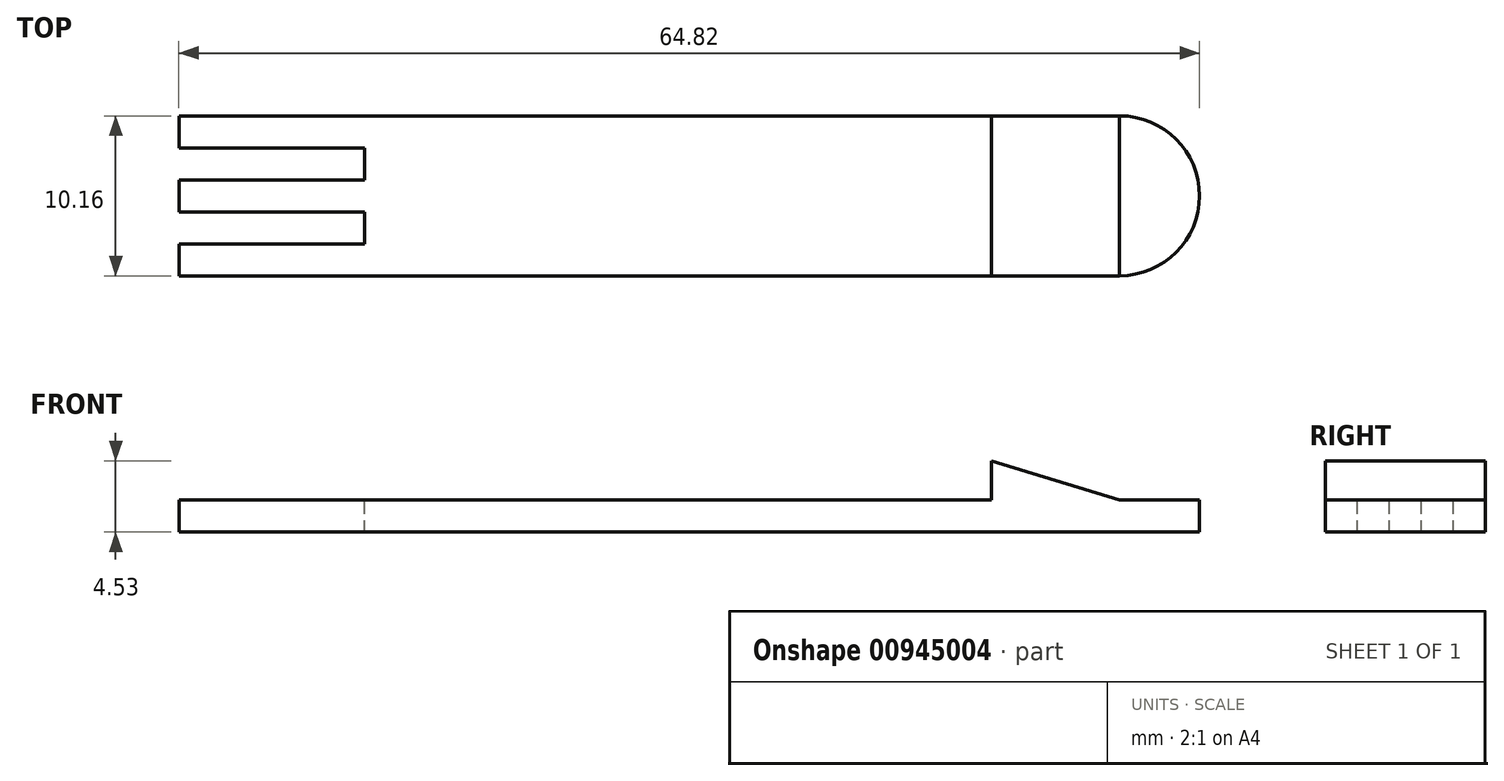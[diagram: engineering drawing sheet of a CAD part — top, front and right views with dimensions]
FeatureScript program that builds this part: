
annotation { "Feature Type Name" : "Feature", "Feature Type Description" : "" }
export const myFeature = defineFeature(function(context is Context, id is Id, definition is map)
    precondition{}
    {
        {
            var Q0;
            Q0=qCreatedBy(makeId("Top.planeOp"),FACE);
            var sketch = newSketch(context, id + "F0", { "sketchPlane" : qUnion([Q0])});
            skLineSegment(sketch, "E0.bottom", {"start": v(-19.76, -30.4) * mm, "end": v(39.98, -30.4) * mm});
            skLineSegment(sketch, "E0.top", {"start": v(-19.76, -40.55) * mm, "end": v(39.98, -40.55) * mm});
            skLineSegment(sketch, "E0.left", {"start": v(-19.76, -30.4) * mm, "end": v(-19.76, -40.55) * mm});
            skLineSegment(sketch, "E0.right", {"start": v(39.98, -30.4) * mm, "end": v(39.98, -40.55) * mm});
            skArc(sketch, "E1", {"start": v(39.98, -40.55) * mm, "mid": v(45.06, -35.47) * mm, "end": v(39.98, -30.4) * mm});
            skSolve(sketch);
        }
        {
            var Q0;
            Q0=qSketchRegion(id+"F0",true);
            extrude(context, id + "F1", {"entities" : qUnion([Q0]), "depth" : 2.03 * mm, "offsetDistance" : 25.4 * mm});
        }
        {
            var Q0;
            Q0=makeQuery(id+"F1.opExtrude","CAP_FACE",FACE,{"disambiguationData":[OSD([sQuery(id+"F0.wireOp",EDGE,"E0.bottom"),sQuery(id+"F0.wireOp",EDGE,"E0.top"),sQuery(id+"F0.wireOp",EDGE,"E0.left"),sQuery(id+"F0.wireOp",EDGE,"E1")])],"isStart":false});
            var sketch = newSketch(context, id + "F2", { "sketchPlane" : qUnion([Q0])});
            skLineSegment(sketch, "E2", {"start": v(-19.76, -32.42) * mm, "end": v(-7.97, -32.42) * mm});
            skLineSegment(sketch, "E3", {"start": v(-19.76, -32.42) * mm, "end": v(-19.76, -30.4) * mm});
            skLineSegment(sketch, "E4", {"start": v(-19.76, -30.4) * mm, "end": v(-19.76, -32.42) * mm});
            skLineSegment(sketch, "E5", {"start": v(-19.76, -34.45) * mm, "end": v(-7.97, -34.45) * mm});
            skLineSegment(sketch, "E6", {"start": v(-19.76, -34.45) * mm, "end": v(-19.76, -32.42) * mm});
            skLineSegment(sketch, "E7", {"start": v(-19.76, -36.49) * mm, "end": v(-7.97, -36.49) * mm});
            skLineSegment(sketch, "E8", {"start": v(-19.76, -36.49) * mm, "end": v(-19.76, -34.45) * mm});
            skLineSegment(sketch, "E9", {"start": v(-19.76, -38.52) * mm, "end": v(-7.97, -38.52) * mm});
            skLineSegment(sketch, "E10", {"start": v(-19.76, -38.52) * mm, "end": v(-19.76, -40.55) * mm});
            skLineSegment(sketch, "E11", {"start": v(-19.76, -40.55) * mm, "end": v(-19.76, -38.52) * mm});
            skLineSegment(sketch, "E12", {"start": v(-7.97, -32.42) * mm, "end": v(-7.97, -34.45) * mm});
            skLineSegment(sketch, "E13", {"start": v(-7.97, -36.49) * mm, "end": v(-7.97, -38.52) * mm});
            skSolve(sketch);
        }
        {
            var Q0;
            Q0=makeQuery(id+"F2.imprint","IMPRINT",FACE,{"disambiguationData":[TD([[makeQuery(id+"F2.imprint","IMPRINT",EDGE,{"derivedFrom":sQuery(id+"F2.wireOp",EDGE,"E2")}),-1.0]])]});
            var Q1;
            {var subQ0=sQuery(id+"F2.wireOp",EDGE,"E7");Q1=makeQuery(id+"F2.imprint","IMPRINT",FACE,{"disambiguationData":[TD([[makeQuery(id+"F2.imprint","IMPRINT",EDGE,{"derivedFrom":subQ0}),-1.0]])]});}
            extrude(context, id + "F3", {"entities" : qUnion([Q0, Q1]), "operationType" : NewBodyOperationType.REMOVE, "oppositeDirection" : true, "depth" : 25.4 * mm, "offsetDistance" : 25.4 * mm});
        }
        {
            var Q0;
            Q0=makeQuery(id+"F1.opExtrude","SWEPT_FACE",FACE,{"disambiguationData":[OSD([sQuery(id+"F0.wireOp",EDGE,"E0.top")])]});
            var sketch = newSketch(context, id + "F4", { "sketchPlane" : qUnion([Q0])});
            skLineSegment(sketch, "E14", {"start": v(39.98, 2.03) * mm, "end": v(31.86, 2.03) * mm});
            skLineSegment(sketch, "E15", {"start": v(31.86, 2.03) * mm, "end": v(31.86, 4.53) * mm});
            skLineSegment(sketch, "E16", {"start": v(31.86, 4.53) * mm, "end": v(39.98, 2.03) * mm});
            skSolve(sketch);
        }
        {
            var Q0;
            Q0=qSketchRegion(id+"F4",true);
            extrude(context, id + "F5", {"entities" : qUnion([Q0]), "operationType" : NewBodyOperationType.ADD, "oppositeDirection" : true, "depth" : 10.16 * mm, "offsetDistance" : 25.4 * mm});
        }
    });
